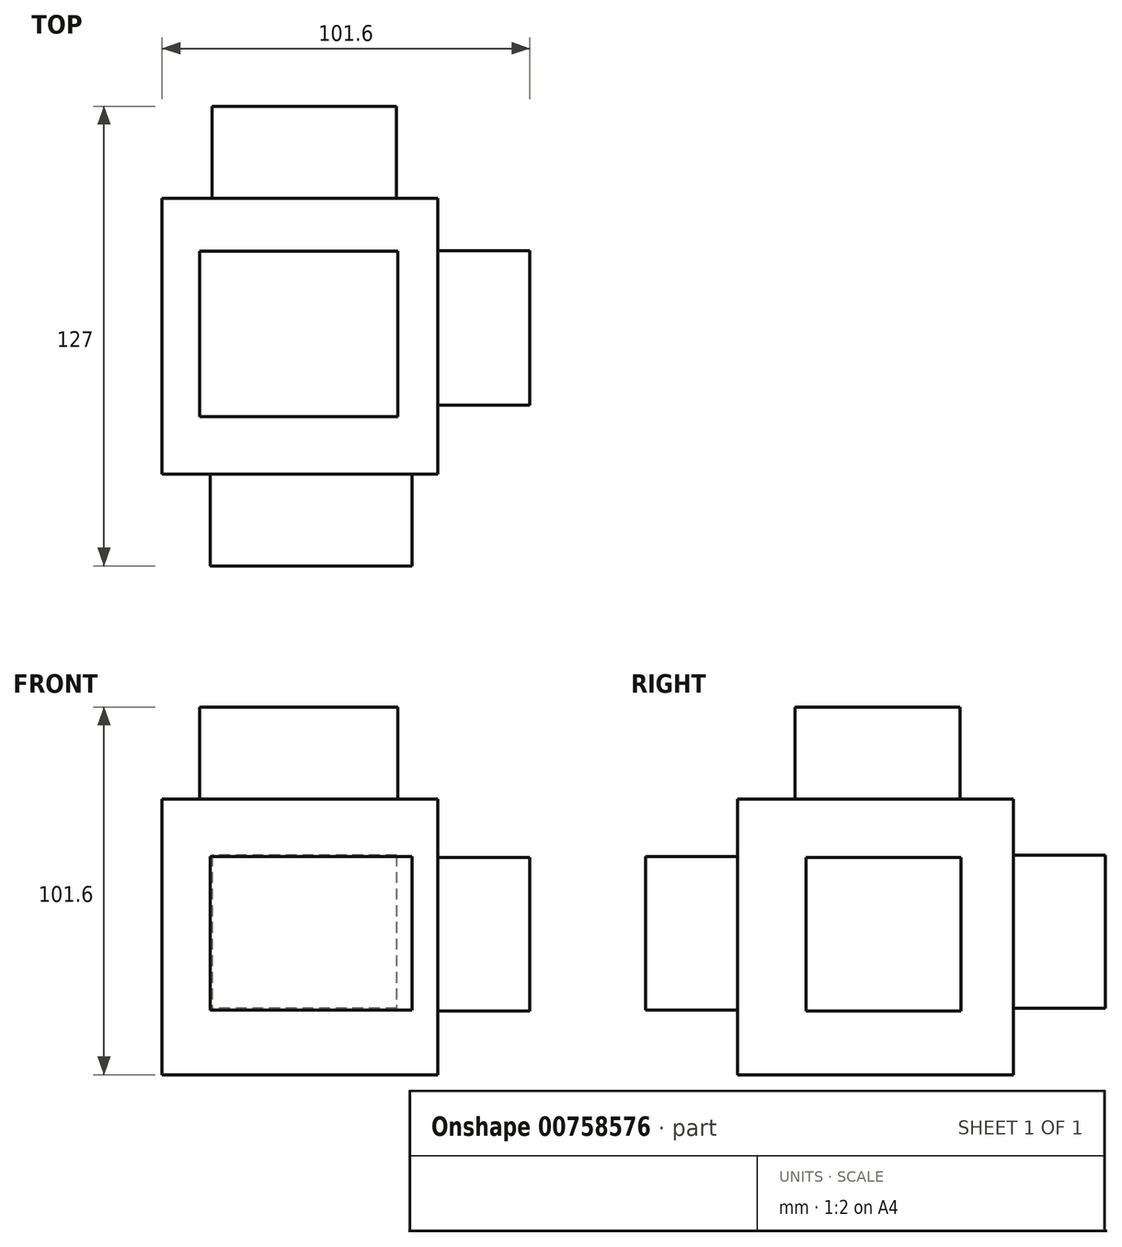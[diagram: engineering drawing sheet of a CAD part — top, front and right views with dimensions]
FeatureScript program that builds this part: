
annotation { "Feature Type Name" : "Feature", "Feature Type Description" : "" }
export const myFeature = defineFeature(function(context is Context, id is Id, definition is map)
    precondition{}
    {
        {
            var Q0;
            Q0=qCreatedBy(makeId("Front.planeOp"),FACE);
            var sketch = newSketch(context, id + "F0", { "sketchPlane" : qUnion([Q0])});
            skLineSegment(sketch, "E0.bottom", {"start": v(-48.53, 50.85) * mm, "end": v(27.67, 50.85) * mm});
            skLineSegment(sketch, "E0.top", {"start": v(-48.53, -25.35) * mm, "end": v(27.67, -25.35) * mm});
            skLineSegment(sketch, "E0.left", {"start": v(-48.53, 50.85) * mm, "end": v(-48.53, -25.35) * mm});
            skLineSegment(sketch, "E0.right", {"start": v(27.67, 50.85) * mm, "end": v(27.67, -25.35) * mm});
            skSolve(sketch);
        }
        {
            var Q0;
            Q0=makeQuery(id+"F0.imprint","IMPRINT",FACE,{"disambiguationData":[TD([[makeQuery(id+"F0.imprint","IMPRINT",EDGE,{"derivedFrom":sQuery(id+"F0.wireOp",EDGE,"E0.bottom")}),-1.0]])]});
            extrude(context, id + "F1", {"entities" : qUnion([Q0]), "depth" : 76.2 * mm, "offsetDistance" : 25.4 * mm});
        }
        {
            var Q0;
            Q0=makeQuery(id+"F1.opExtrude","SWEPT_FACE",FACE,{"disambiguationData":[OSD([sQuery(id+"F0.wireOp",EDGE,"E0.bottom")])]});
            var sketch = newSketch(context, id + "F2", { "sketchPlane" : qUnion([Q0])});
            skLineSegment(sketch, "E1.bottom", {"start": v(-38.11, -14.72) * mm, "end": v(16.57, -14.72) * mm});
            skLineSegment(sketch, "E1.top", {"start": v(-38.11, -60.4) * mm, "end": v(16.57, -60.4) * mm});
            skLineSegment(sketch, "E1.left", {"start": v(-38.11, -14.72) * mm, "end": v(-38.11, -60.4) * mm});
            skLineSegment(sketch, "E1.right", {"start": v(16.57, -14.72) * mm, "end": v(16.57, -60.4) * mm});
            skSolve(sketch);
        }
        {
            var Q0;
            Q0=makeQuery(id+"F2.imprint","IMPRINT",FACE,{"disambiguationData":[TD([[makeQuery(id+"F2.imprint","IMPRINT",EDGE,{"derivedFrom":sQuery(id+"F2.wireOp",EDGE,"E1.bottom")}),-1.0]])]});
            extrude(context, id + "F3", {"entities" : qUnion([Q0]), "operationType" : NewBodyOperationType.ADD, "depth" : 25.4 * mm, "offsetDistance" : 25.4 * mm});
        }
        {
            var Q0;
            Q0=makeQuery(id+"F1.opExtrude","SWEPT_FACE",FACE,{"disambiguationData":[OSD([sQuery(id+"F0.wireOp",EDGE,"E0.right")])]});
            var sketch = newSketch(context, id + "F4", { "sketchPlane" : qUnion([Q0])});
            skLineSegment(sketch, "E2.bottom", {"start": v(-57.25, 34.62) * mm, "end": v(-14.53, 34.62) * mm});
            skLineSegment(sketch, "E2.top", {"start": v(-57.25, -7.72) * mm, "end": v(-14.53, -7.72) * mm});
            skLineSegment(sketch, "E2.left", {"start": v(-57.25, 34.62) * mm, "end": v(-57.25, -7.72) * mm});
            skLineSegment(sketch, "E2.right", {"start": v(-14.53, 34.62) * mm, "end": v(-14.53, -7.72) * mm});
            skSolve(sketch);
        }
        {
            var Q0;
            Q0=makeQuery(id+"F4.imprint","IMPRINT",FACE,{"disambiguationData":[TD([[makeQuery(id+"F4.imprint","IMPRINT",EDGE,{"derivedFrom":sQuery(id+"F4.wireOp",EDGE,"E2.bottom")}),-1.0]])]});
            extrude(context, id + "F5", {"entities" : qUnion([Q0]), "operationType" : NewBodyOperationType.ADD, "depth" : 25.4 * mm, "offsetDistance" : 25.4 * mm});
        }
        {
            var Q0;
            Q0=makeQuery(id+"F1.opExtrude","CAP_FACE",FACE,{"disambiguationData":[OSD([sQuery(id+"F0.wireOp",EDGE,"E0.bottom"),sQuery(id+"F0.wireOp",EDGE,"E0.top"),sQuery(id+"F0.wireOp",EDGE,"E0.left"),sQuery(id+"F0.wireOp",EDGE,"E0.right")])],"isStart":false});
            var sketch = newSketch(context, id + "F6", { "sketchPlane" : qUnion([Q0])});
            skLineSegment(sketch, "E3.bottom", {"start": v(-35.2, 34.87) * mm, "end": v(20.54, 34.87) * mm});
            skLineSegment(sketch, "E3.top", {"start": v(-35.2, -7.47) * mm, "end": v(20.54, -7.47) * mm});
            skLineSegment(sketch, "E3.left", {"start": v(-35.2, 34.87) * mm, "end": v(-35.2, -7.47) * mm});
            skLineSegment(sketch, "E3.right", {"start": v(20.54, 34.87) * mm, "end": v(20.54, -7.47) * mm});
            skSolve(sketch);
        }
        {
            var Q0;
            Q0=makeQuery(id+"F6.imprint","IMPRINT",FACE,{"disambiguationData":[TD([[makeQuery(id+"F6.imprint","IMPRINT",EDGE,{"derivedFrom":sQuery(id+"F6.wireOp",EDGE,"E3.bottom")}),-1.0]])]});
            extrude(context, id + "F7", {"entities" : qUnion([Q0]), "operationType" : NewBodyOperationType.ADD, "depth" : 25.4 * mm, "offsetDistance" : 25.4 * mm});
        }
        {
            var Q0;
            Q0=makeQuery(id+"F1.opExtrude","CAP_FACE",FACE,{"disambiguationData":[OSD([sQuery(id+"F0.wireOp",EDGE,"E0.bottom"),sQuery(id+"F0.wireOp",EDGE,"E0.top"),sQuery(id+"F0.wireOp",EDGE,"E0.left"),sQuery(id+"F0.wireOp",EDGE,"E0.right")])],"isStart":true});
            var sketch = newSketch(context, id + "F8", { "sketchPlane" : qUnion([Q0])});
            skLineSegment(sketch, "E4.bottom", {"start": v(-16.24, 35.25) * mm, "end": v(34.7, 35.25) * mm});
            skLineSegment(sketch, "E4.top", {"start": v(-16.24, -6.97) * mm, "end": v(34.7, -6.97) * mm});
            skLineSegment(sketch, "E4.left", {"start": v(-16.24, 35.25) * mm, "end": v(-16.24, -6.97) * mm});
            skLineSegment(sketch, "E4.right", {"start": v(34.7, 35.25) * mm, "end": v(34.7, -6.97) * mm});
            skSolve(sketch);
        }
        {
            var Q0;
            Q0=makeQuery(id+"F8.imprint","IMPRINT",FACE,{"disambiguationData":[TD([[makeQuery(id+"F8.imprint","IMPRINT",EDGE,{"derivedFrom":sQuery(id+"F8.wireOp",EDGE,"E4.bottom")}),-1.0]])]});
            extrude(context, id + "F9", {"entities" : qUnion([Q0]), "operationType" : NewBodyOperationType.ADD, "depth" : 25.4 * mm, "offsetDistance" : 25.4 * mm});
        }
    });
